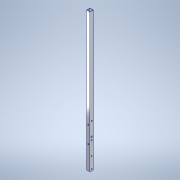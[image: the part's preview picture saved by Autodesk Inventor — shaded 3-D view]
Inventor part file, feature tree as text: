
AUTODESK INVENTOR PART (.ipt)
format: ipt  version: 2020.3 (Build 243373000, 373)  size: 181,760 bytes
history: native  units: mm
features: sketch x8, extrude x4, hole x4, other x1
ambient origin geometry x8: Origin, YZ Plane, XZ Plane, XY Plane, X Axis, Y Axis, Z Axis, Center Point
bodies: Body1 (feature_tree)
feature tree (17):
  other  "ソリッド1"
  extrude  "押し出し1"  Depth=9.0mm
  hole  "穴1"  [1 undecoded]
  hole  "穴2"  [1 undecoded]
  hole  "穴3"  [1 undecoded]
  extrude  "押し出し2"  Depth=1.2mm
  extrude  "押し出し3"  Depth=1.2mm
  hole  "穴4"  [1 undecoded]
  extrude  "押し出し4"  Depth=4.5mm
  sketch  "スケッチ1"
  sketch  "スケッチ2"
  sketch  "スケッチ3"
  sketch  "スケッチ4"
  sketch  "スケッチ5"
  sketch  "スケッチ6"
  sketch  "スケッチ7"
  sketch  "スケッチ8"
note: 4 required parameter values undecoded (feature->parameter linkage not recoverable at this tier; creation-order binding heuristic only, values carry confidence <= 0.55)
